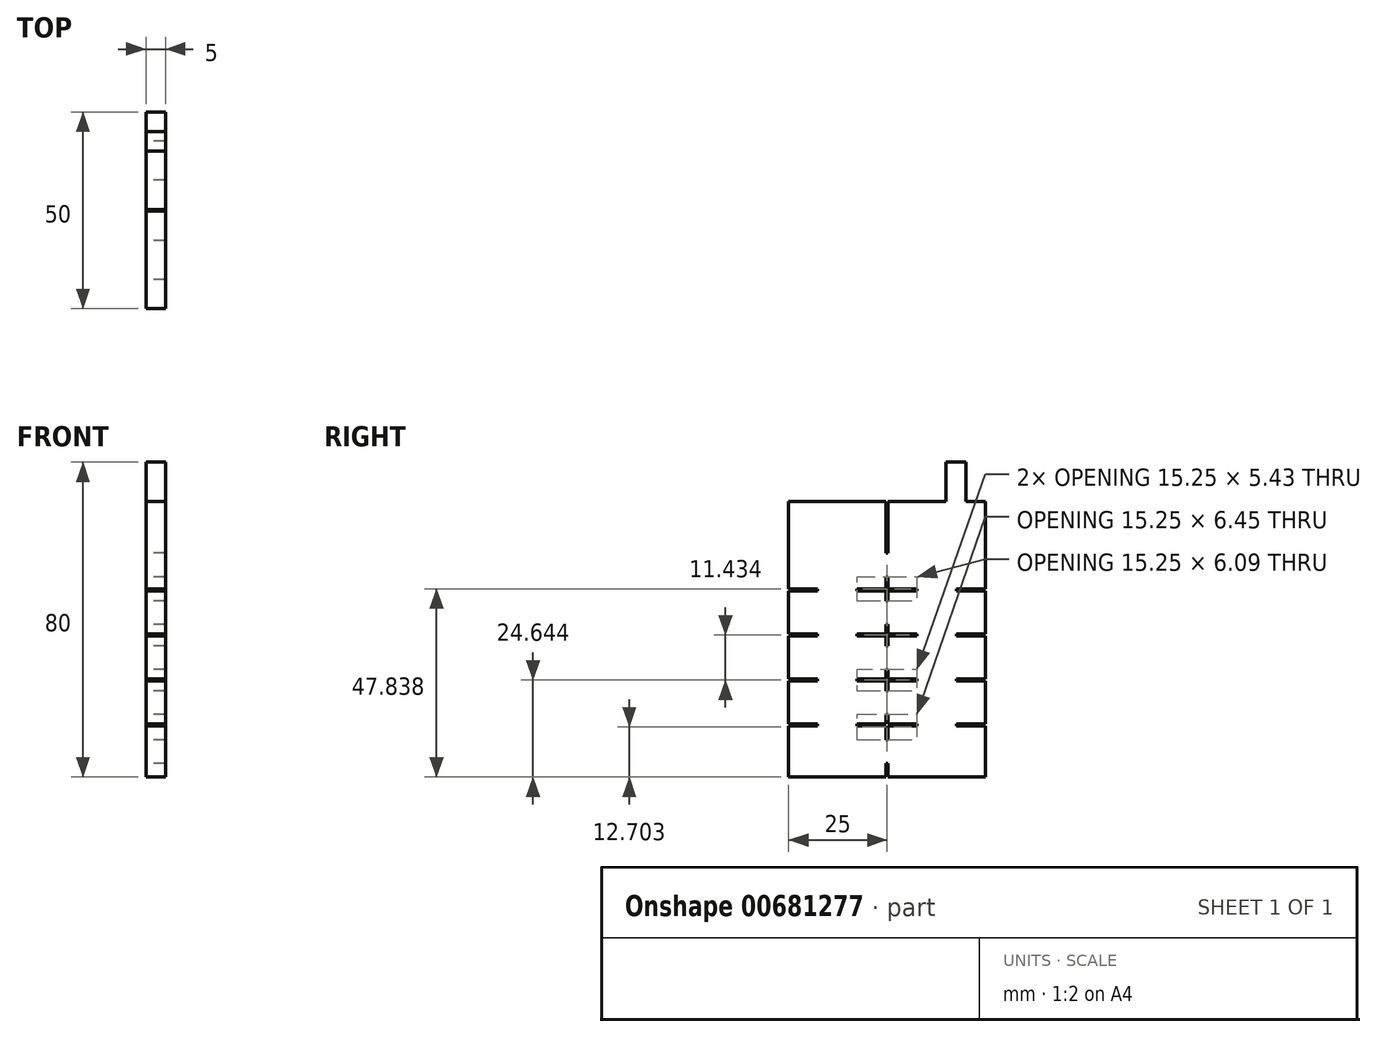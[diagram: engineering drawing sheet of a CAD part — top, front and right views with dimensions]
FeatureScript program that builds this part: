
annotation { "Feature Type Name" : "Feature", "Feature Type Description" : "" }
export const myFeature = defineFeature(function(context is Context, id is Id, definition is map)
    precondition{}
    {
        {
            var Q0;
            Q0=qCreatedBy(makeId("Right.planeOp"),FACE);
            var sketch = newSketch(context, id + "F0", { "sketchPlane" : qUnion([Q0])});
            skPoint(sketch, "E0.0", {"position": v(0, 0) * mm});
            skLineSegment(sketch, "E1.bottom", {"start": v(0, 0) * mm, "end": v(12.38, 0) * mm});
            skLineSegment(sketch, "E1.top", {"start": v(0, -60) * mm, "end": v(24.75, -60) * mm});
            skLineSegment(sketch, "E1.left", {"start": v(0, 0) * mm, "end": v(0, -12.24) * mm});
            skLineSegment(sketch, "E1.right", {"start": v(50, 0) * mm, "end": v(50, -12.24) * mm});
            skPoint(sketch, "E2.MirrorP", {"position": v(11.5, 0) * mm});
            skPoint(sketch, "E3.MirrorP", {"position": v(11.5, -2) * mm});
            skPoint(sketch, "E4.MirrorP", {"position": v(18.5, 0) * mm});
            skPoint(sketch, "E5.MirrorP", {"position": v(30, 0) * mm});
            skLineSegment(sketch, "E6.0", {"start": v(25.25, -60) * mm, "end": v(25.25, -56.52) * mm});
            skLineSegment(sketch, "E7.0", {"start": v(0, -12.24) * mm, "end": v(7.38, -12.24) * mm});
            skLineSegment(sketch, "E8.0", {"start": v(0, -12.74) * mm, "end": v(7.38, -12.74) * mm});
            skLineSegment(sketch, "E9.trimOffspring", {"start": v(25.25, -3.12) * mm, "end": v(25.25, -1.3) * mm});
            skLineSegment(sketch, "E10.trimOffspring", {"start": v(25.25, -12.24) * mm, "end": v(32.63, -12.24) * mm});
            skLineSegment(sketch, "E11.trimOffspring", {"start": v(25.25, -12.24) * mm, "end": v(25.25, -9.12) * mm});
            skLineSegment(sketch, "E12.trimOffspring", {"start": v(25.25, -12.74) * mm, "end": v(32.63, -12.74) * mm});
            skLineSegment(sketch, "E13.trimOffspring", {"start": v(25.25, -15.2) * mm, "end": v(25.25, -12.74) * mm});
            skLineSegment(sketch, "E14.0", {"start": v(0, -23.67) * mm, "end": v(7.38, -23.67) * mm});
            skLineSegment(sketch, "E15.0", {"start": v(0, -24.17) * mm, "end": v(7.38, -24.17) * mm});
            skLineSegment(sketch, "E16.trimOffspring", {"start": v(25.25, -23.67) * mm, "end": v(32.63, -23.67) * mm});
            skLineSegment(sketch, "E17.trimOffspring", {"start": v(25.25, -23.67) * mm, "end": v(25.25, -21.2) * mm});
            skLineSegment(sketch, "E18.trimOffspring", {"start": v(25.25, -24.17) * mm, "end": v(32.63, -24.17) * mm});
            skLineSegment(sketch, "E19.trimOffspring", {"start": v(25.25, -26.64) * mm, "end": v(25.25, -24.17) * mm});
            skLineSegment(sketch, "E20.trimOffspring", {"start": v(24.75, -26.64) * mm, "end": v(24.75, -24.17) * mm});
            skLineSegment(sketch, "E21.0", {"start": v(0, -35.1) * mm, "end": v(7.38, -35.1) * mm});
            skLineSegment(sketch, "E22.0", {"start": v(0, -35.6) * mm, "end": v(7.38, -35.6) * mm});
            skLineSegment(sketch, "E23.trimOffspring", {"start": v(25.25, -35.1) * mm, "end": v(32.63, -35.1) * mm});
            skLineSegment(sketch, "E24.trimOffspring", {"start": v(25.25, -35.1) * mm, "end": v(25.25, -32.64) * mm});
            skLineSegment(sketch, "E25.trimOffspring", {"start": v(24.75, -35.1) * mm, "end": v(24.75, -32.64) * mm});
            skLineSegment(sketch, "E26.trimOffspring", {"start": v(25.25, -35.6) * mm, "end": v(32.63, -35.6) * mm});
            skLineSegment(sketch, "E27.trimOffspring", {"start": v(25.25, -38.07) * mm, "end": v(25.25, -35.6) * mm});
            skLineSegment(sketch, "E28.trimOffspring", {"start": v(24.75, -38.07) * mm, "end": v(24.75, -35.6) * mm});
            skLineSegment(sketch, "E29.0", {"start": v(0, -46.54) * mm, "end": v(7.38, -46.54) * mm});
            skLineSegment(sketch, "E30.0", {"start": v(0, -47.04) * mm, "end": v(7.38, -47.04) * mm});
            skLineSegment(sketch, "E31.trimOffspring", {"start": v(25.25, -46.54) * mm, "end": v(32.63, -46.54) * mm});
            skLineSegment(sketch, "E32.trimOffspring", {"start": v(25.25, -46.54) * mm, "end": v(25.25, -44.07) * mm});
            skLineSegment(sketch, "E33.trimOffspring", {"start": v(24.75, -46.54) * mm, "end": v(24.75, -44.07) * mm});
            skLineSegment(sketch, "E34.trimOffspring", {"start": v(25.25, -47.04) * mm, "end": v(32.63, -47.04) * mm});
            skLineSegment(sketch, "E35.trimOffspring", {"start": v(25.25, -50.52) * mm, "end": v(25.25, -47.04) * mm});
            skLineSegment(sketch, "E36.trimOffspring", {"start": v(0, -12.74) * mm, "end": v(0, -23.67) * mm});
            skLineSegment(sketch, "E37.trimOffspring", {"start": v(0, -24.17) * mm, "end": v(0, -35.1) * mm});
            skLineSegment(sketch, "E38.trimOffspring", {"start": v(0, -35.6) * mm, "end": v(0, -46.54) * mm});
            skLineSegment(sketch, "E39.trimOffspring", {"start": v(0, -47.04) * mm, "end": v(0, -60) * mm});
            skLineSegment(sketch, "E40.trimOffspring", {"start": v(50, -47.04) * mm, "end": v(50, -60) * mm});
            skLineSegment(sketch, "E41.trimOffspring", {"start": v(50, -35.6) * mm, "end": v(50, -46.54) * mm});
            skLineSegment(sketch, "E42.trimOffspring", {"start": v(50, -12.74) * mm, "end": v(50, -23.67) * mm});
            skLineSegment(sketch, "E43.trimOffspring", {"start": v(50, -24.17) * mm, "end": v(50, -35.1) * mm});
            skLineSegment(sketch, "E44.0", {"start": v(17.38, -12.74) * mm, "end": v(17.38, -12.24) * mm});
            skLineSegment(sketch, "E45.0", {"start": v(7.38, -12.74) * mm, "end": v(7.38, -12.24) * mm});
            skLineSegment(sketch, "E46", {"start": v(24.75, -12.24) * mm, "end": v(24.75, -9.12) * mm});
            skLineSegment(sketch, "E47.0", {"start": v(24.75, -9.12) * mm, "end": v(25.25, -9.12) * mm});
            skLineSegment(sketch, "E48.0", {"start": v(24.75, -3.12) * mm, "end": v(25.25, -3.12) * mm});
            skLineSegment(sketch, "E49", {"start": v(24.75, -12.74) * mm, "end": v(24.75, -15.2) * mm});
            skLineSegment(sketch, "E50.0", {"start": v(24.75, -21.2) * mm, "end": v(25.25, -21.2) * mm});
            skLineSegment(sketch, "E51.0", {"start": v(24.75, -15.2) * mm, "end": v(25.25, -15.2) * mm});
            skLineSegment(sketch, "E52", {"start": v(25.25, -1.3) * mm, "end": v(25.25, 0) * mm});
            skLineSegment(sketch, "E53.trimOffspring", {"start": v(25.25, 0) * mm, "end": v(35.12, 0) * mm});
            skPoint(sketch, "E54.start.orphan", {"position": v(24.75, -6.12) * mm});
            skLineSegment(sketch, "E55", {"start": v(7.38, -12.24) * mm, "end": v(7.38, -12.74) * mm});
            skLineSegment(sketch, "E56", {"start": v(17.38, -12.24) * mm, "end": v(17.38, -12.74) * mm});
            skLineSegment(sketch, "E57.trimOffspring", {"start": v(7.38, -23.67) * mm, "end": v(7.38, -24.17) * mm});
            skLineSegment(sketch, "E58.trimOffspring", {"start": v(17.38, -23.67) * mm, "end": v(17.38, -24.17) * mm});
            skLineSegment(sketch, "E59.trimOffspring", {"start": v(7.38, -35.1) * mm, "end": v(7.38, -35.6) * mm});
            skLineSegment(sketch, "E60.trimOffspring", {"start": v(17.38, -35.1) * mm, "end": v(17.38, -35.6) * mm});
            skLineSegment(sketch, "E61.trimOffspring", {"start": v(7.38, -46.54) * mm, "end": v(7.38, -47.04) * mm});
            skLineSegment(sketch, "E62.trimOffspring", {"start": v(17.38, -46.54) * mm, "end": v(17.38, -47.04) * mm});
            skLineSegment(sketch, "E63.trimOffspring", {"start": v(17.38, -46.54) * mm, "end": v(24.75, -46.54) * mm});
            skLineSegment(sketch, "E64.trimOffspring", {"start": v(17.38, -47.04) * mm, "end": v(24.75, -47.04) * mm});
            skLineSegment(sketch, "E65.trimOffspring", {"start": v(17.38, -35.1) * mm, "end": v(24.75, -35.1) * mm});
            skLineSegment(sketch, "E66.trimOffspring", {"start": v(17.38, -35.6) * mm, "end": v(24.75, -35.6) * mm});
            skLineSegment(sketch, "E67.trimOffspring", {"start": v(17.37, -23.67) * mm, "end": v(24.75, -23.67) * mm});
            skLineSegment(sketch, "E68.trimOffspring", {"start": v(17.37, -24.17) * mm, "end": v(24.75, -24.17) * mm});
            skLineSegment(sketch, "E69.trimOffspring", {"start": v(17.38, -12.24) * mm, "end": v(24.75, -12.24) * mm});
            skPoint(sketch, "E70.start.orphan", {"position": v(12.38, -12.74) * mm});
            skPoint(sketch, "E71.orphan", {"position": v(12.38, -12.24) * mm});
            skLineSegment(sketch, "E72.trimOffspring", {"start": v(17.38, -12.74) * mm, "end": v(24.75, -12.74) * mm});
            skLineSegment(sketch, "E73.0", {"start": v(32.63, -12.24) * mm, "end": v(32.63, -12.74) * mm});
            skLineSegment(sketch, "E74.0", {"start": v(42.62, -12.24) * mm, "end": v(42.62, -12.74) * mm});
            skLineSegment(sketch, "E75.trimOffspring", {"start": v(32.63, -23.67) * mm, "end": v(32.63, -24.17) * mm});
            skLineSegment(sketch, "E76.trimOffspring", {"start": v(42.62, -23.67) * mm, "end": v(42.62, -24.17) * mm});
            skLineSegment(sketch, "E77.trimOffspring", {"start": v(32.63, -35.1) * mm, "end": v(32.63, -35.6) * mm});
            skLineSegment(sketch, "E78.trimOffspring", {"start": v(42.62, -35.1) * mm, "end": v(42.62, -35.6) * mm});
            skLineSegment(sketch, "E79.trimOffspring", {"start": v(32.63, -46.54) * mm, "end": v(32.63, -47.04) * mm});
            skLineSegment(sketch, "E80.trimOffspring", {"start": v(42.62, -46.54) * mm, "end": v(42.62, -47.04) * mm});
            skLineSegment(sketch, "E81.0", {"start": v(24.75, -26.64) * mm, "end": v(25.25, -26.64) * mm});
            skLineSegment(sketch, "E82.0", {"start": v(24.75, -32.64) * mm, "end": v(25.25, -32.64) * mm});
            skLineSegment(sketch, "E83.0", {"start": v(24.75, -38.07) * mm, "end": v(25.25, -38.07) * mm});
            skLineSegment(sketch, "E84.0", {"start": v(24.75, -44.07) * mm, "end": v(25.25, -44.07) * mm});
            skLineSegment(sketch, "E85", {"start": v(24.75, -47.04) * mm, "end": v(24.75, -50.52) * mm});
            skLineSegment(sketch, "E86.0", {"start": v(24.75, -56.52) * mm, "end": v(25.25, -56.52) * mm});
            skLineSegment(sketch, "E87.0", {"start": v(24.75, -50.52) * mm, "end": v(25.25, -50.52) * mm});
            skLineSegment(sketch, "E88.trimOffspring", {"start": v(24.75, -56.52) * mm, "end": v(24.75, -60) * mm});
            skLineSegment(sketch, "E89.trimOffspring", {"start": v(25.25, -60) * mm, "end": v(50, -60) * mm});
            skLineSegment(sketch, "E90.trimOffspring", {"start": v(42.62, -46.54) * mm, "end": v(50, -46.54) * mm});
            skLineSegment(sketch, "E91.trimOffspring", {"start": v(42.62, -47.04) * mm, "end": v(50, -47.04) * mm});
            skLineSegment(sketch, "E92.trimOffspring", {"start": v(42.62, -35.1) * mm, "end": v(50, -35.1) * mm});
            skLineSegment(sketch, "E93.trimOffspring", {"start": v(42.62, -35.6) * mm, "end": v(50, -35.6) * mm});
            skLineSegment(sketch, "E94.trimOffspring", {"start": v(42.62, -23.67) * mm, "end": v(50, -23.67) * mm});
            skLineSegment(sketch, "E95.trimOffspring", {"start": v(42.62, -24.17) * mm, "end": v(50, -24.17) * mm});
            skLineSegment(sketch, "E96.trimOffspring", {"start": v(42.62, -12.24) * mm, "end": v(50, -12.24) * mm});
            skLineSegment(sketch, "E97.trimOffspring", {"start": v(42.62, -12.74) * mm, "end": v(50, -12.74) * mm});
            skLineSegment(sketch, "E98.trimOffspring", {"start": v(24.75, -21.2) * mm, "end": v(24.75, -23.67) * mm});
            skPoint(sketch, "E99.end.orphan", {"position": v(25.25, -18.2) * mm});
            skPoint(sketch, "E99.start.orphan", {"position": v(24.75, -18.2) * mm});
            skPoint(sketch, "E100.orphan", {"position": v(25.25, -17.95) * mm});
            skPoint(sketch, "E101.end.orphan", {"position": v(25.25, -18.45) * mm});
            skLineSegment(sketch, "E102.trimOffspring", {"start": v(24.75, -3.12) * mm, "end": v(24.75, 0) * mm});
            skPoint(sketch, "E103.orphan", {"position": v(14.88, 25) * mm});
            skPoint(sketch, "E104.orphan", {"position": v(37.63, 25) * mm});
            skLineSegment(sketch, "E105.trimOffspring", {"start": v(14.88, 0) * mm, "end": v(24.75, 0) * mm});
            skLineSegment(sketch, "E106.trimOffspring", {"start": v(37.63, 0) * mm, "end": v(40, 0) * mm});
            skLineSegment(sketch, "E107", {"start": v(35.12, 0) * mm, "end": v(40, 0) * mm});
            skLineSegment(sketch, "E108.0", {"start": v(45, 0) * mm, "end": v(45, 15) * mm});
            skLineSegment(sketch, "E109.0", {"start": v(40, 0) * mm, "end": v(40, 15) * mm});
            skLineSegment(sketch, "E110", {"start": v(14.88, 0) * mm, "end": v(11.5, 0) * mm});
            skLineSegment(sketch, "E111.trimOffspring", {"start": v(45, 0) * mm, "end": v(50, 0) * mm});
            skLineSegment(sketch, "E112.0", {"start": v(40, 20) * mm, "end": v(45, 20) * mm});
            skLineSegment(sketch, "E113", {"start": v(40, 20) * mm, "end": v(40, 15) * mm});
            skLineSegment(sketch, "E114", {"start": v(45, 20) * mm, "end": v(45, 15) * mm});
            skSolve(sketch);
        }
        {
            var Q0;
            {var subQ1=sQuery(id+"F0.wireOp",EDGE,"6f222dcf-cafe-427f-96f1-de862232ba62.0");Q0=makeQuery(id+"F0.imprint","IMPRINT",FACE,{"disambiguationData":[TD([[makeQuery(id+"F0.imprint","IMPRINT",EDGE,{"derivedFrom":subQ1}),-1.0]])]});}
            var Q1;
            {var subQ1=sQuery(id+"F0.wireOp",EDGE,"9ddca581-0f96-48d2-9b8e-d0e5be099db1.trimOffspring");Q1=makeQuery(id+"F0.imprint","IMPRINT",FACE,{"disambiguationData":[TD([[makeQuery(id+"F0.imprint","IMPRINT",EDGE,{"derivedFrom":subQ1}),-1.0]])]});}
            var Q2;
            Q2=makeQuery(id+"F0.imprint","IMPRINT",FACE,{"disambiguationData":[TD([[makeQuery(id+"F0.imprint","IMPRINT",EDGE,{"derivedFrom":sQuery(id+"F0.wireOp",EDGE,"E8.0")}),-1.0]])]});
            var Q3;
            Q3=makeQuery(id+"F0.imprint","IMPRINT",FACE,{"disambiguationData":[TD([[makeQuery(id+"F0.imprint","IMPRINT",EDGE,{"derivedFrom":sQuery(id+"F0.wireOp",EDGE,"E12.trimOffspring")}),-1.0]])]});
            var Q4;
            Q4=makeQuery(id+"F0.imprint","IMPRINT",FACE,{"disambiguationData":[TD([[makeQuery(id+"F0.imprint","IMPRINT",EDGE,{"derivedFrom":sQuery(id+"F0.wireOp",EDGE,"E18.trimOffspring")}),-1.0]])]});
            var Q5;
            Q5=makeQuery(id+"F0.imprint","IMPRINT",FACE,{"disambiguationData":[TD([[makeQuery(id+"F0.imprint","IMPRINT",EDGE,{"derivedFrom":sQuery(id+"F0.wireOp",EDGE,"E15.0")}),-1.0]])]});
            var Q6;
            Q6=makeQuery(id+"F0.imprint","IMPRINT",FACE,{"disambiguationData":[TD([[makeQuery(id+"F0.imprint","IMPRINT",EDGE,{"derivedFrom":sQuery(id+"F0.wireOp",EDGE,"E22.0")}),-1.0]])]});
            var Q7;
            Q7=makeQuery(id+"F0.imprint","IMPRINT",FACE,{"disambiguationData":[TD([[makeQuery(id+"F0.imprint","IMPRINT",EDGE,{"derivedFrom":sQuery(id+"F0.wireOp",EDGE,"E26.trimOffspring")}),-1.0]])]});
            var Q8;
            {var subQ0=sQuery(id+"F0.wireOp",EDGE,"E6.0");Q8=makeQuery(id+"F0.imprint","IMPRINT",FACE,{"disambiguationData":[TD([[makeQuery(id+"F0.imprint","IMPRINT",EDGE,{"derivedFrom":subQ0}),-1.0]])]});}
            var Q9;
            {var subQ0=sQuery(id+"F0.wireOp",EDGE,"52d86100-12cc-4532-affd-39e9c9b04a49.0");Q9=makeQuery(id+"F0.imprint","IMPRINT",FACE,{"disambiguationData":[TD([[makeQuery(id+"F0.imprint","IMPRINT",EDGE,{"derivedFrom":subQ0}),1.0]])]});}
            extrude(context, id + "F1", {"entities" : qUnion([Q0, Q1, Q2, Q3, Q4, Q5, Q6, Q7, Q8, Q9]), "depth" : 5 * mm, "offsetDistance" : 25 * mm});
        }
        {
            var Q0;
            Q0=makeQuery(id+"F1.opExtrude","SWEPT_FACE",FACE,{"disambiguationData":[OSD([sQuery(id+"F0.wireOp",EDGE,"E53.trimOffspring"),sQuery(id+"F0.wireOp",EDGE,"E107")])]});
            var Q1;
            Q1=makeQuery(id+"F1.opExtrude","SWEPT_FACE",FACE,{"disambiguationData":[OSD([sQuery(id+"F0.wireOp",EDGE,"E1.bottom"),sQuery(id+"F0.wireOp",EDGE,"E105.trimOffspring"),sQuery(id+"F0.wireOp",EDGE,"E110")])]});
            var Q2;
            Q2=makeQuery(id+"F1.opExtrude","SWEPT_FACE",FACE,{"disambiguationData":[OSD([sQuery(id+"F0.wireOp",EDGE,"E111.trimOffspring")])]});
            extrude(context, id + "F2", {"entities" : qUnion([Q0, Q1, Q2]), "operationType" : NewBodyOperationType.ADD, "depth" : 10 * mm, "offsetDistance" : 25 * mm});
        }
    });
